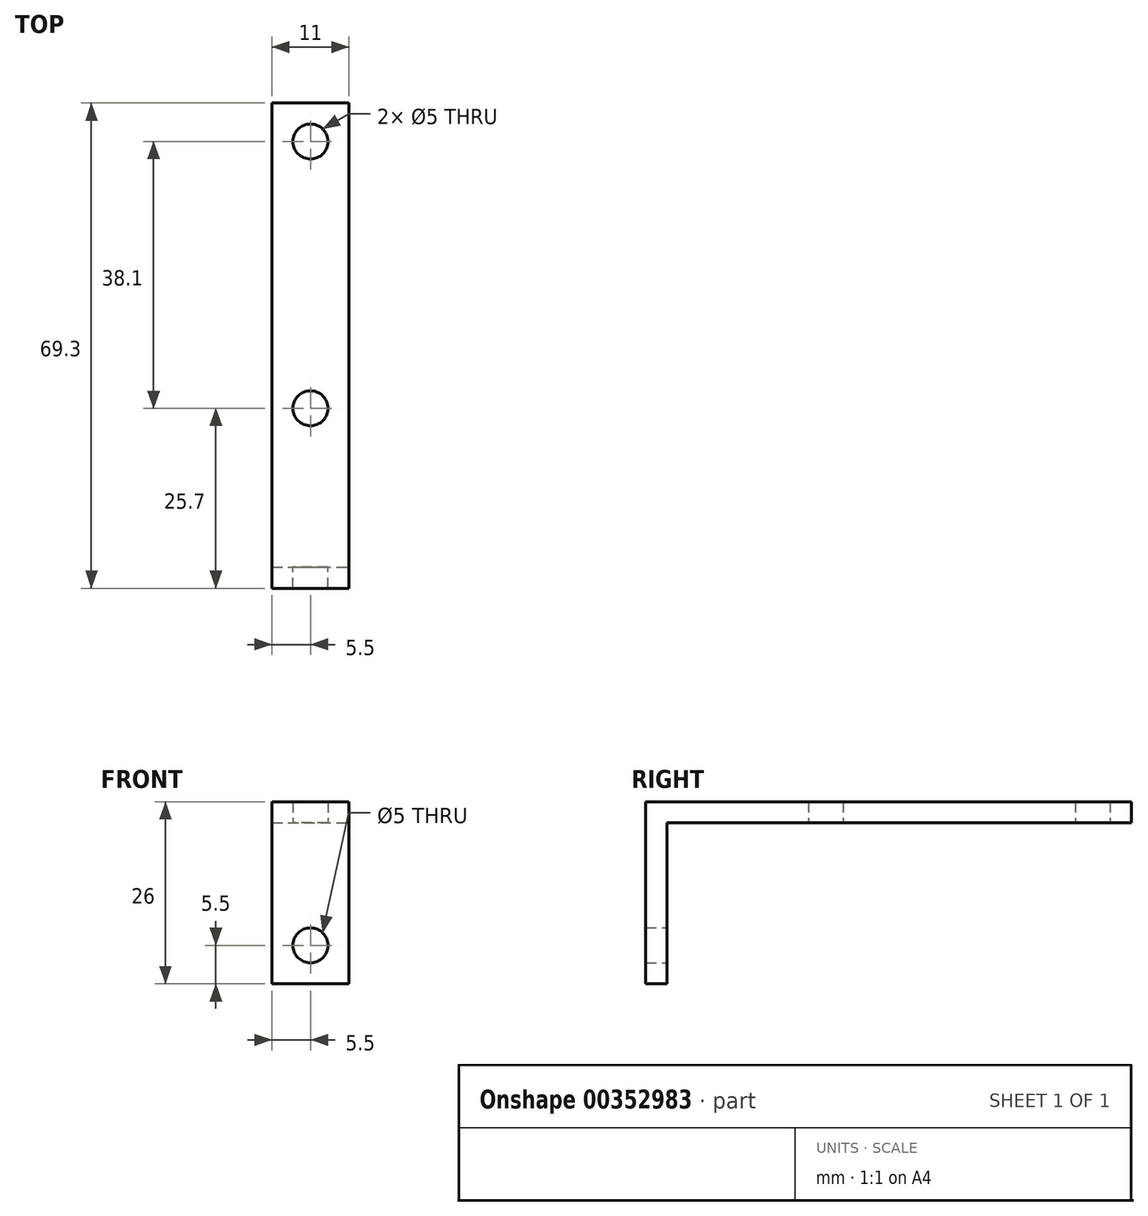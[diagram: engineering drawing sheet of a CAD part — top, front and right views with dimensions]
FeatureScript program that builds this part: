
annotation { "Feature Type Name" : "Feature", "Feature Type Description" : "" }
export const myFeature = defineFeature(function(context is Context, id is Id, definition is map)
    precondition{}
    {
        {
            assignVariable(context, id + "F0", {"name" : "wand", "anyValue" : 3});
        }
        {
            var Q0;
            Q0=qCreatedBy(makeId("Top.planeOp"),FACE);
            var sketch = newSketch(context, id + "F1", { "sketchPlane" : qUnion([Q0])});
            skLineSegment(sketch, "E0.bottom", {"start": v(-5.5, 66.3) * mm, "end": v(5.5, 66.3) * mm});
            skLineSegment(sketch, "E0.top", {"start": v(-5.5, 0) * mm, "end": v(5.5, 0) * mm});
            skLineSegment(sketch, "E0.left", {"start": v(-5.5, 66.3) * mm, "end": v(-5.5, 0) * mm});
            skLineSegment(sketch, "E0.right", {"start": v(5.5, 66.3) * mm, "end": v(5.5, 0) * mm});
            skCircle(sketch, "E1", {"center": v(0, 22.7) * mm, "radius": 2.5 * mm});
            skCircle(sketch, "E2", {"center": v(0, 60.8) * mm, "radius": 2.5 * mm});
            skSolve(sketch);
        }
        {
            var Q0;
            Q0 = qSketchRegion(id + "F1", true);
            extrude(context, id + "F2", {"entities" : qUnion([Q0]), "depth" : (getVariable(context, 'wand')) * mm});
        }
        {
            var Q0;
            Q0=qCreatedBy(makeId("Front.planeOp"),FACE);
            var sketch = newSketch(context, id + "F3", { "sketchPlane" : qUnion([Q0])});
            skLineSegment(sketch, "E3.0.1", {"start": v(5.5, 0) * mm, "end": v(5.5, 3) * mm});
            skLineSegment(sketch, "E3.0.2", {"start": v(5.5, 3) * mm, "end": v(-5.5, 3) * mm});
            skLineSegment(sketch, "E3.0.3", {"start": v(-5.5, 3) * mm, "end": v(-5.5, 0) * mm});
            skLineSegment(sketch, "E4.bottom", {"start": v(-5.5, 3) * mm, "end": v(5.5, 3) * mm});
            skLineSegment(sketch, "E4.top", {"start": v(-5.5, -23) * mm, "end": v(5.5, -23) * mm});
            skLineSegment(sketch, "E4.left", {"start": v(-5.5, 3) * mm, "end": v(-5.5, -23) * mm});
            skLineSegment(sketch, "E4.right", {"start": v(5.5, 3) * mm, "end": v(5.5, -23) * mm});
            skPoint(sketch, "E5.1", {"position": v(0, 0) * mm});
            skLineSegment(sketch, "E6.0", {"start": v(-5.5, 0) * mm, "end": v(5.5, 0) * mm, "construction": true});
            skCircle(sketch, "E7", {"center": v(0, -17.5) * mm, "radius": 2.5 * mm});
            skSolve(sketch);
        }
        {
            var Q0;
            Q0 = qSketchRegion(id + "F3", true);
            extrude(context, id + "F4", {"entities" : qUnion([Q0]), "operationType" : NewBodyOperationType.ADD, "depth" : (getVariable(context, 'wand')) * mm});
        }
    });
